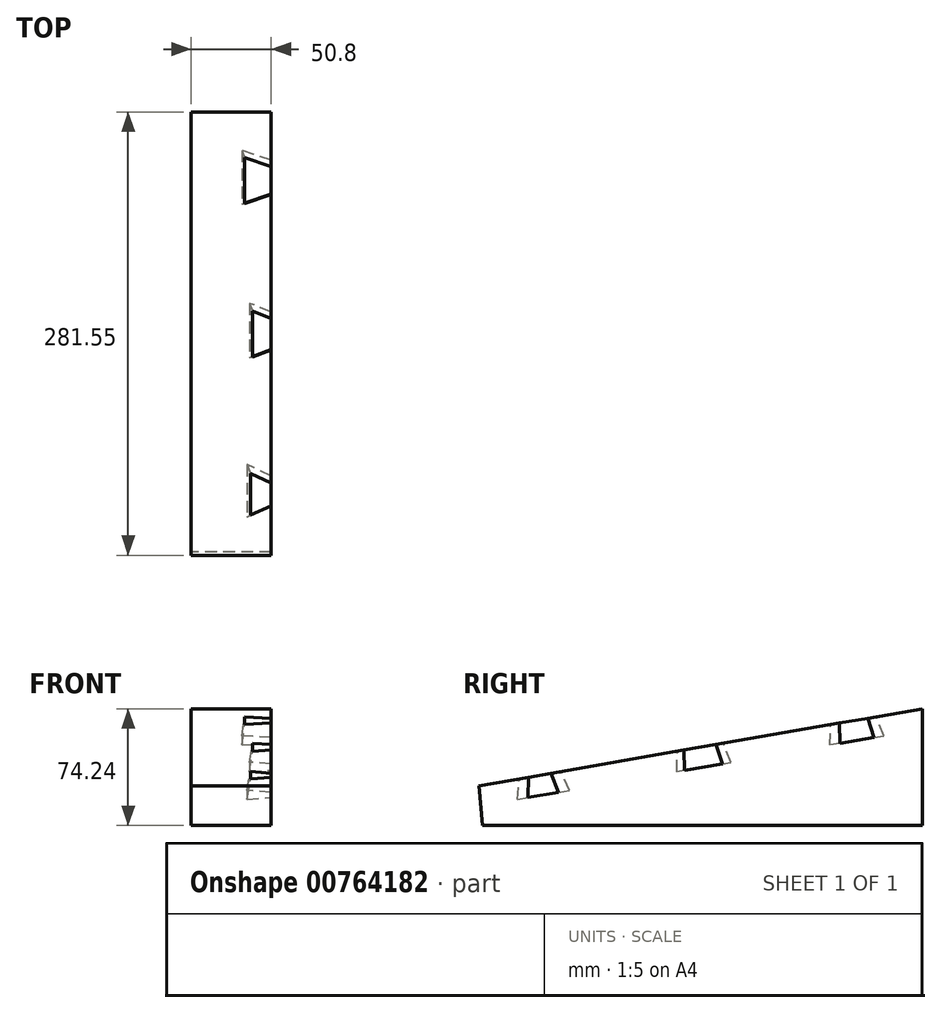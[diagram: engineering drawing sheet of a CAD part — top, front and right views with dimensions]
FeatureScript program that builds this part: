
annotation { "Feature Type Name" : "Feature", "Feature Type Description" : "" }
export const myFeature = defineFeature(function(context is Context, id is Id, definition is map)
    precondition{}
    {
        {
            var Q0;
            Q0=qCreatedBy(makeId("Right.planeOp"),FACE);
            var sketch = newSketch(context, id + "F0", { "sketchPlane" : qUnion([Q0])});
            skLineSegment(sketch, "E0", {"start": v(-138.66, -24.61) * mm, "end": v(140.74, -24.61) * mm});
            skLineSegment(sketch, "E1", {"start": v(140.74, -24.61) * mm, "end": v(140.74, 49.63) * mm});
            skLineSegment(sketch, "E2", {"start": v(140.74, 49.63) * mm, "end": v(-140.81, 0.7) * mm});
            skLineSegment(sketch, "E3", {"start": v(-140.81, 0.7) * mm, "end": v(-138.66, -24.61) * mm});
            skSolve(sketch);
        }
        {
            var Q0;
            Q0=makeQuery(id+"F0.imprint","IMPRINT",FACE,{"disambiguationData":[TD([[makeQuery(id+"F0.imprint","IMPRINT",EDGE,{"derivedFrom":sQuery(id+"F0.wireOp",EDGE,"E0")}),1.0]])]});
            extrude(context, id + "F1", {"entities" : qUnion([Q0]), "depth" : 50.8 * mm, "offsetDistance" : 25.4 * mm});
        }
        {
            var Q0;
            Q0=makeQuery(id+"F1.opExtrude","SWEPT_FACE",FACE,{"disambiguationData":[OSD([sQuery(id+"F0.wireOp",EDGE,"E2")])]});
            var sketch = newSketch(context, id + "F2", { "sketchPlane" : qUnion([Q0])});
            skSolve(sketch);
        }
        {
            var Q0;
            {var subQ0=sQuery(id+"F0.wireOp",EDGE,"E2");Q0=makeQuery(id+"F2.imprint","IMPRINT",FACE,{"disambiguationData":[TD([[makeQuery(id+"F2.imprint","IMPRINT",EDGE,{"derivedFrom":makeQuery(id+"F1.opExtrude","CAP_EDGE",EDGE,{"disambiguationData":[OSD([subQ0])],"isStart":true})}),1.0]])]});}
            var sketch = newSketch(context, id + "F3", { "sketchPlane" : qUnion([Q0])});
            skLineSegment(sketch, "E4.MirrorCS", {"start": v(33.91, 88.07) * mm, "end": v(33.91, 117.66) * mm});
            skLineSegment(sketch, "E5.MirrorCS", {"start": v(33.91, 117.66) * mm, "end": v(50.8, 112.08) * mm});
            skLineSegment(sketch, "E6.MirrorCS", {"start": v(50.8, 93.78) * mm, "end": v(33.91, 88.07) * mm});
            skLineSegment(sketch, "E7.MirrorCS", {"start": v(38.89, 18.9) * mm, "end": v(50.8, 14.14) * mm});
            skLineSegment(sketch, "E8.MirrorCS", {"start": v(50.8, -6.46) * mm, "end": v(38.89, -10.7) * mm});
            skLineSegment(sketch, "E9.MirrorCS", {"start": v(38.89, -10.7) * mm, "end": v(38.89, 18.9) * mm});
            skLineSegment(sketch, "E10.MirrorCS", {"start": v(31.58, -90.48) * mm, "end": v(50.8, -95.85) * mm});
            skLineSegment(sketch, "E11.MirrorCS", {"start": v(50.8, -114.14) * mm, "end": v(31.57, -120.23) * mm});
            skLineSegment(sketch, "E12.MirrorCS", {"start": v(31.57, -120.23) * mm, "end": v(31.57, -90.48) * mm});
            skLineSegment(sketch, "E13", {"start": v(50.8, -114.14) * mm, "end": v(50.8, -95.85) * mm});
            skSolve(sketch);
        }
        {
            var Q0;
            Q0=makeQuery(id+"F3.imprint","IMPRINT",FACE,{"disambiguationData":[TD([[makeQuery(id+"F3.imprint","IMPRINT",EDGE,{"derivedFrom":sQuery(id+"F3.wireOp",EDGE,"E4.MirrorCS")}),-1.0]])]});
            var Q1;
            {var subQ0=sQuery(id+"F3.wireOp",EDGE,"E7.MirrorCS");Q1=makeQuery(id+"F3.imprint","IMPRINT",FACE,{"disambiguationData":[TD([[makeQuery(id+"F3.imprint","IMPRINT",EDGE,{"derivedFrom":subQ0}),-1.0]])]});}
            extrude(context, id + "F4", {"entities" : qUnion([Q0, Q1]), "operationType" : NewBodyOperationType.REMOVE, "oppositeDirection" : true, "depth" : 12.7 * mm, "offsetDistance" : 25.4 * mm, "hasDraft" : true, "draftAngle" : 8 * degree});
        }
        {
            var Q0;
            {var subQ0=sQuery(id+"F0.wireOp",EDGE,"E2");Q0=makeQuery(id+"F2.imprint","IMPRINT",FACE,{"disambiguationData":[TD([[makeQuery(id+"F2.imprint","IMPRINT",EDGE,{"derivedFrom":makeQuery(id+"F1.opExtrude","CAP_EDGE",EDGE,{"disambiguationData":[OSD([subQ0])],"isStart":true})}),1.0]])]});}
            var sketch = newSketch(context, id + "F5", { "sketchPlane" : qUnion([Q0])});
            skLineSegment(sketch, "E14", {"start": v(50.8, -106.7) * mm, "end": v(37.66, -112.63) * mm});
            skLineSegment(sketch, "E15", {"start": v(37.66, -112.63) * mm, "end": v(37.66, -85.97) * mm});
            skLineSegment(sketch, "E16", {"start": v(37.66, -85.97) * mm, "end": v(50.8, -92.06) * mm});
            skSolve(sketch);
        }
        {
            var Q0;
            {var subQ0=sQuery(id+"F5.wireOp",EDGE,"E14");Q0=makeQuery(id+"F5.imprint","IMPRINT",FACE,{"disambiguationData":[TD([[makeQuery(id+"F5.imprint","IMPRINT",EDGE,{"derivedFrom":subQ0}),-1.0]])]});}
            extrude(context, id + "F6", {"entities" : qUnion([Q0]), "operationType" : NewBodyOperationType.REMOVE, "oppositeDirection" : true, "depth" : 12.7 * mm, "offsetDistance" : 25.4 * mm, "hasDraft" : true, "draftAngle" : 10 * degree});
        }
    });
